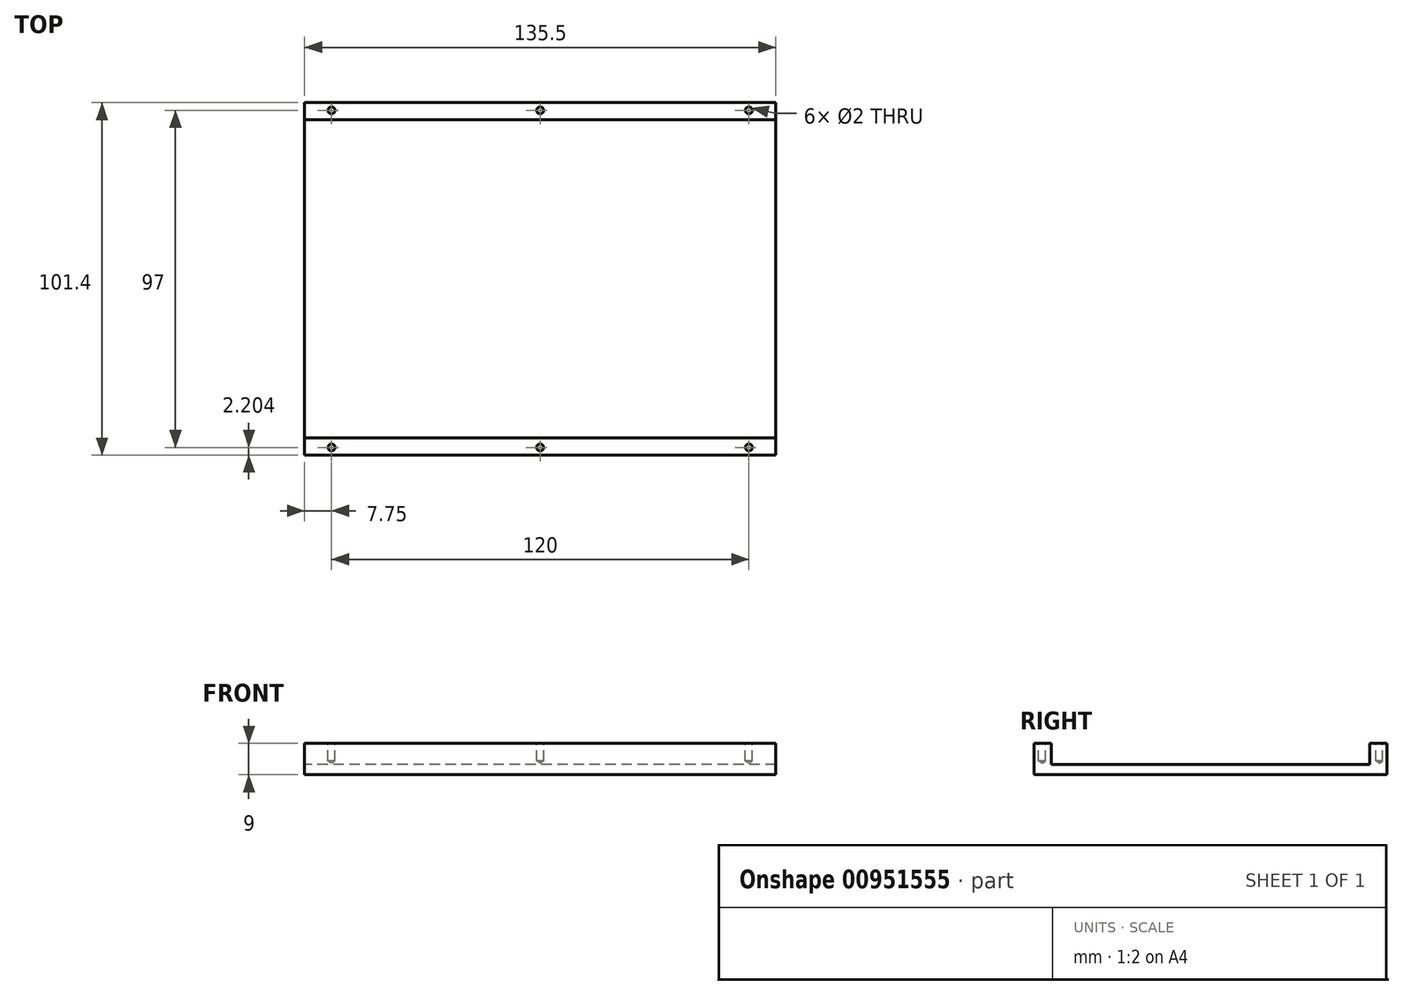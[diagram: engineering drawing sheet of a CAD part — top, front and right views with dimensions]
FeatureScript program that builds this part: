
annotation { "Feature Type Name" : "Feature", "Feature Type Description" : "" }
export const myFeature = defineFeature(function(context is Context, id is Id, definition is map)
    precondition{}
    {
        {
            var Q0;
            Q0=qCreatedBy(makeId("Top.planeOp"),FACE);
            var sketch = newSketch(context, id + "F0", { "sketchPlane" : qUnion([Q0])});
            skLineSegment(sketch, "E0.bottom", {"start": v(-69.44, 72.02) * mm, "end": v(66.06, 72.02) * mm});
            skLineSegment(sketch, "E0.top", {"start": v(-69.44, -29.38) * mm, "end": v(66.06, -29.38) * mm});
            skLineSegment(sketch, "E0.left", {"start": v(-69.44, 72.02) * mm, "end": v(-69.44, -29.38) * mm});
            skLineSegment(sketch, "E0.right", {"start": v(66.06, 72.02) * mm, "end": v(66.06, -29.38) * mm});
            skSolve(sketch);
        }
        {
            var Q0;
            Q0=makeQuery(id+"F0.imprint","IMPRINT",FACE,{"disambiguationData":[TD([[makeQuery(id+"F0.imprint","IMPRINT",EDGE,{"derivedFrom":sQuery(id+"F0.wireOp",EDGE,"E0.bottom")}),-1.0]])]});
            extrude(context, id + "F1", {"entities" : qUnion([Q0]), "depth" : 3 * mm, "offsetDistance" : 25 * mm});
        }
        {
            var Q0;
            Q0=makeQuery(id+"F1.opExtrude","CAP_FACE",FACE,{"disambiguationData":[OSD([sQuery(id+"F0.wireOp",EDGE,"E0.bottom"),sQuery(id+"F0.wireOp",EDGE,"E0.top"),sQuery(id+"F0.wireOp",EDGE,"E0.left"),sQuery(id+"F0.wireOp",EDGE,"E0.right")])],"isStart":false});
            var sketch = newSketch(context, id + "F2", { "sketchPlane" : qUnion([Q0])});
            skLineSegment(sketch, "E1.bottom", {"start": v(-69.44, -24.48) * mm, "end": v(66.06, -24.48) * mm});
            skLineSegment(sketch, "E1.top", {"start": v(-69.44, -29.38) * mm, "end": v(66.06, -29.38) * mm});
            skLineSegment(sketch, "E1.left", {"start": v(-69.44, -24.48) * mm, "end": v(-69.44, -29.38) * mm});
            skLineSegment(sketch, "E1.right", {"start": v(66.06, -24.48) * mm, "end": v(66.06, -29.38) * mm});
            skLineSegment(sketch, "E2.bottom", {"start": v(66.06, 72.02) * mm, "end": v(-69.44, 72.02) * mm});
            skLineSegment(sketch, "E2.top", {"start": v(66.06, 67.12) * mm, "end": v(-69.44, 67.12) * mm});
            skLineSegment(sketch, "E2.left", {"start": v(66.06, 72.02) * mm, "end": v(66.06, 67.12) * mm});
            skLineSegment(sketch, "E2.right", {"start": v(-69.44, 72.02) * mm, "end": v(-69.44, 67.12) * mm});
            skSolve(sketch);
        }
        {
            var Q0;
            Q0=makeQuery(id+"F2.imprint","IMPRINT",FACE,{"disambiguationData":[TD([[makeQuery(id+"F2.imprint","IMPRINT",EDGE,{"derivedFrom":sQuery(id+"F2.wireOp",EDGE,"E1.bottom")}),-1.0]])]});
            extrude(context, id + "F3", {"entities" : qUnion([Q0]), "operationType" : NewBodyOperationType.ADD, "depth" : 6 * mm, "offsetDistance" : 25 * mm});
        }
        {
            var Q0;
            Q0 = qSketchRegion(id + "F2", true);
            extrude(context, id + "F4", {"entities" : qUnion([Q0]), "operationType" : NewBodyOperationType.ADD, "depth" : 6 * mm, "offsetDistance" : 25 * mm});
        }
        {
            var Q0;
            Q0=makeQuery(id+"F3.opExtrude","CAP_FACE",FACE,{"disambiguationData":[OSD([sQuery(id+"F2.wireOp",EDGE,"E1.bottom"),sQuery(id+"F2.wireOp",EDGE,"E1.top"),sQuery(id+"F2.wireOp",EDGE,"E1.left"),sQuery(id+"F2.wireOp",EDGE,"E1.right")])],"isStart":false});
            var sketch = newSketch(context, id + "F5", { "sketchPlane" : qUnion([Q0])});
            skPoint(sketch, "E3", {"position": v(-61.69, -27.18) * mm});
            skPoint(sketch, "E4", {"position": v(-1.69, -27.18) * mm});
            skPoint(sketch, "E5", {"position": v(58.31, -27.18) * mm});
            skPoint(sketch, "E6", {"position": v(58.31, 69.82) * mm});
            skPoint(sketch, "E7", {"position": v(-1.69, 69.82) * mm});
            skPoint(sketch, "E8", {"position": v(-61.69, 69.82) * mm});
            skSolve(sketch);
        }
        {
            var Q0;
            Q0=sQuery(id+"F5.wireOp",VERTEX,"E8");
            var Q1;
            Q1=sQuery(id+"F5.wireOp",VERTEX,"E7");
            var Q2;
            Q2=sQuery(id+"F5.wireOp",VERTEX,"E6");
            var Q3;
            Q3=sQuery(id+"F5.wireOp",VERTEX,"E5");
            var Q4;
            Q4=sQuery(id+"F5.wireOp",VERTEX,"E4");
            var Q5;
            Q5=sQuery(id+"F5.wireOp",VERTEX,"E3");
            var Q6;
            Q6=makeQuery(id+"F1.opExtrude","SWEPT_BODY",BODY,{"disambiguationData":[OSD([sQuery(id+"F0.wireOp",EDGE,"E0.bottom"),sQuery(id+"F0.wireOp",EDGE,"E0.top"),sQuery(id+"F0.wireOp",EDGE,"E0.left"),sQuery(id+"F0.wireOp",EDGE,"E0.right")])]});
            hole(context, id + "F6", {"style" : HoleStyle.SIMPLE, "endStyle" : HoleEndStyle.BLIND, "holeDiameter" : 2 * mm, "majorDiameter" : 5 * mm, "holeDepth" : 5 * mm, "isTappedThrough" : true, "tappedDepth" : 12 * mm, "tapClearance" : 3, "locations" : qUnion([Q0, Q1, Q2, Q3, Q4, Q5]), "scope" : qUnion([Q6])});
        }
    });
